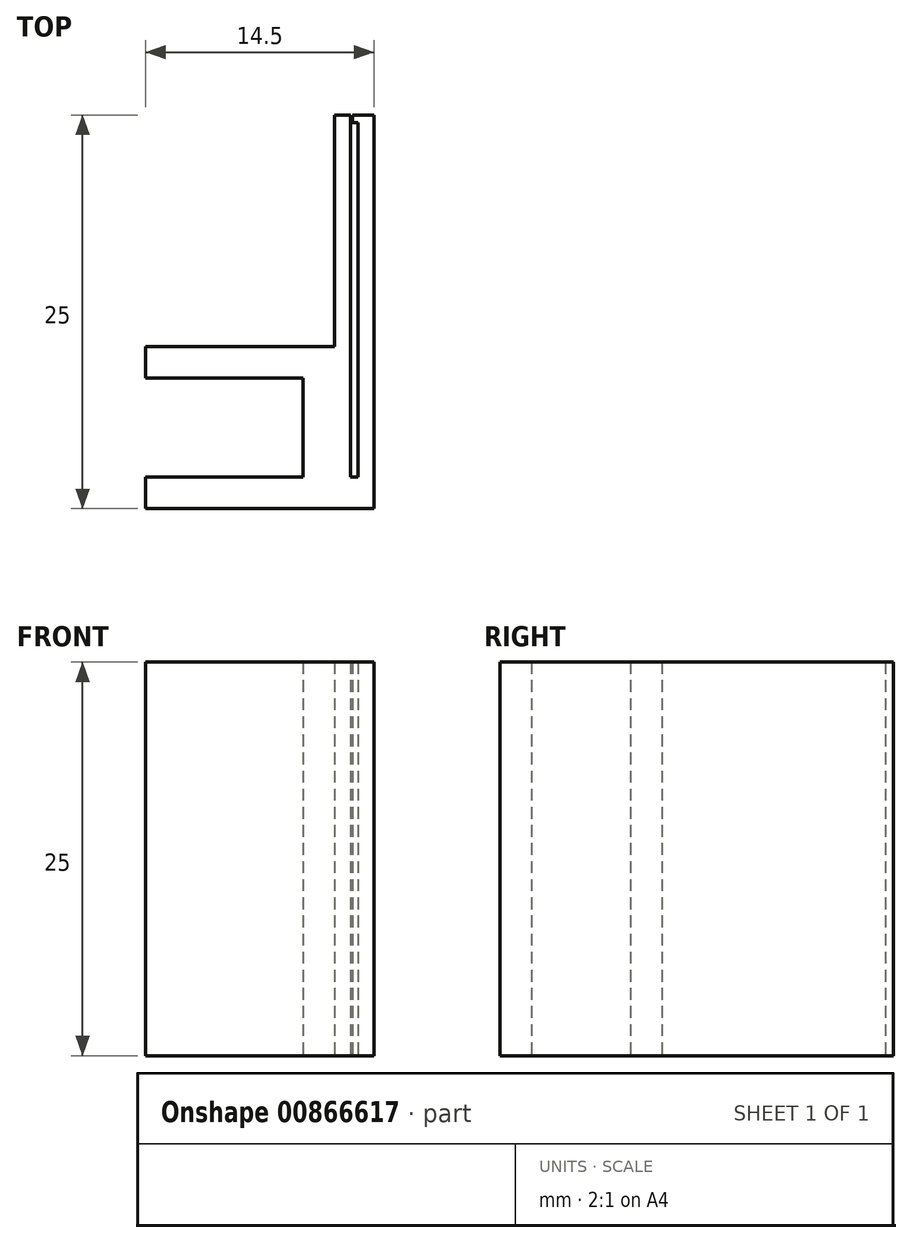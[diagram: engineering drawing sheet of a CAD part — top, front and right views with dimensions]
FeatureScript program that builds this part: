
annotation { "Feature Type Name" : "Feature", "Feature Type Description" : "" }
export const myFeature = defineFeature(function(context is Context, id is Id, definition is map)
    precondition{}
    {
        {
            var Q0;
            Q0=qCreatedBy(makeId("Top.planeOp"),FACE);
            var sketch = newSketch(context, id + "F0", { "sketchPlane" : qUnion([Q0])});
            skLineSegment(sketch, "E0.bottom", {"start": v(-10, 5.15) * mm, "end": v(2, 5.15) * mm});
            skLineSegment(sketch, "E0.top", {"start": v(-10, 3.15) * mm, "end": v(2, 3.15) * mm});
            skLineSegment(sketch, "E0.left", {"start": v(-10, 5.15) * mm, "end": v(-10, 3.15) * mm});
            skLineSegment(sketch, "E0.right", {"start": v(2, 5.15) * mm, "end": v(2, 3.15) * mm});
            skLineSegment(sketch, "E1.bottom", {"start": v(-10, -3.15) * mm, "end": v(2, -3.15) * mm});
            skLineSegment(sketch, "E1.top", {"start": v(-10, -5.15) * mm, "end": v(2, -5.15) * mm});
            skLineSegment(sketch, "E1.left", {"start": v(-10, -3.15) * mm, "end": v(-10, -5.15) * mm});
            skLineSegment(sketch, "E1.right", {"start": v(2, -3.15) * mm, "end": v(2, -5.15) * mm});
            skLineSegment(sketch, "E2.bottom", {"start": v(0, 3.15) * mm, "end": v(2, 3.15) * mm});
            skLineSegment(sketch, "E2.top", {"start": v(0, -3.15) * mm, "end": v(2, -3.15) * mm});
            skLineSegment(sketch, "E2.left", {"start": v(0, 3.15) * mm, "end": v(0, -3.15) * mm});
            skLineSegment(sketch, "E2.right", {"start": v(2, 3.15) * mm, "end": v(2, -3.15) * mm});
            skLineSegment(sketch, "E3", {"start": v(2, -5.15) * mm, "end": v(2, 19.85) * mm});
            skLineSegment(sketch, "E4", {"start": v(2, 19.85) * mm, "end": v(3, 19.85) * mm});
            skLineSegment(sketch, "E5", {"start": v(3, 19.85) * mm, "end": v(3, -5.15) * mm});
            skLineSegment(sketch, "E6", {"start": v(3, -5.15) * mm, "end": v(2, -5.15) * mm});
            skLineSegment(sketch, "E7", {"start": v(3, -5.15) * mm, "end": v(3.5, -5.15) * mm});
            skLineSegment(sketch, "E8", {"start": v(3.5, -5.15) * mm, "end": v(3.5, -3.15) * mm});
            skLineSegment(sketch, "E9", {"start": v(3.5, -3.15) * mm, "end": v(3, -3.15) * mm});
            skLineSegment(sketch, "E10", {"start": v(3.5, -5.15) * mm, "end": v(4.5, -5.15) * mm});
            skLineSegment(sketch, "E11", {"start": v(4.5, -5.15) * mm, "end": v(4.5, 19.85) * mm});
            skLineSegment(sketch, "E12", {"start": v(4.5, 19.85) * mm, "end": v(3.5, 19.85) * mm});
            skLineSegment(sketch, "E13", {"start": v(3.5, 19.85) * mm, "end": v(3.5, -3.15) * mm});
            skLineSegment(sketch, "E14.bottom", {"start": v(3.5, 19.85) * mm, "end": v(3.15, 19.85) * mm});
            skLineSegment(sketch, "E14.top", {"start": v(3.5, 19.35) * mm, "end": v(3.15, 19.35) * mm});
            skLineSegment(sketch, "E14.left", {"start": v(3.5, 19.85) * mm, "end": v(3.5, 19.35) * mm});
            skLineSegment(sketch, "E14.right", {"start": v(3.15, 19.85) * mm, "end": v(3.15, 19.35) * mm});
            skSolve(sketch);
        }
        {
            var Q0;
            Q0 = qSketchRegion(id + "F0", true);
            extrude(context, id + "F1", {"entities" : qUnion([Q0]), "depth" : 25 * mm, "offsetDistance" : 25 * mm});
        }
    });
